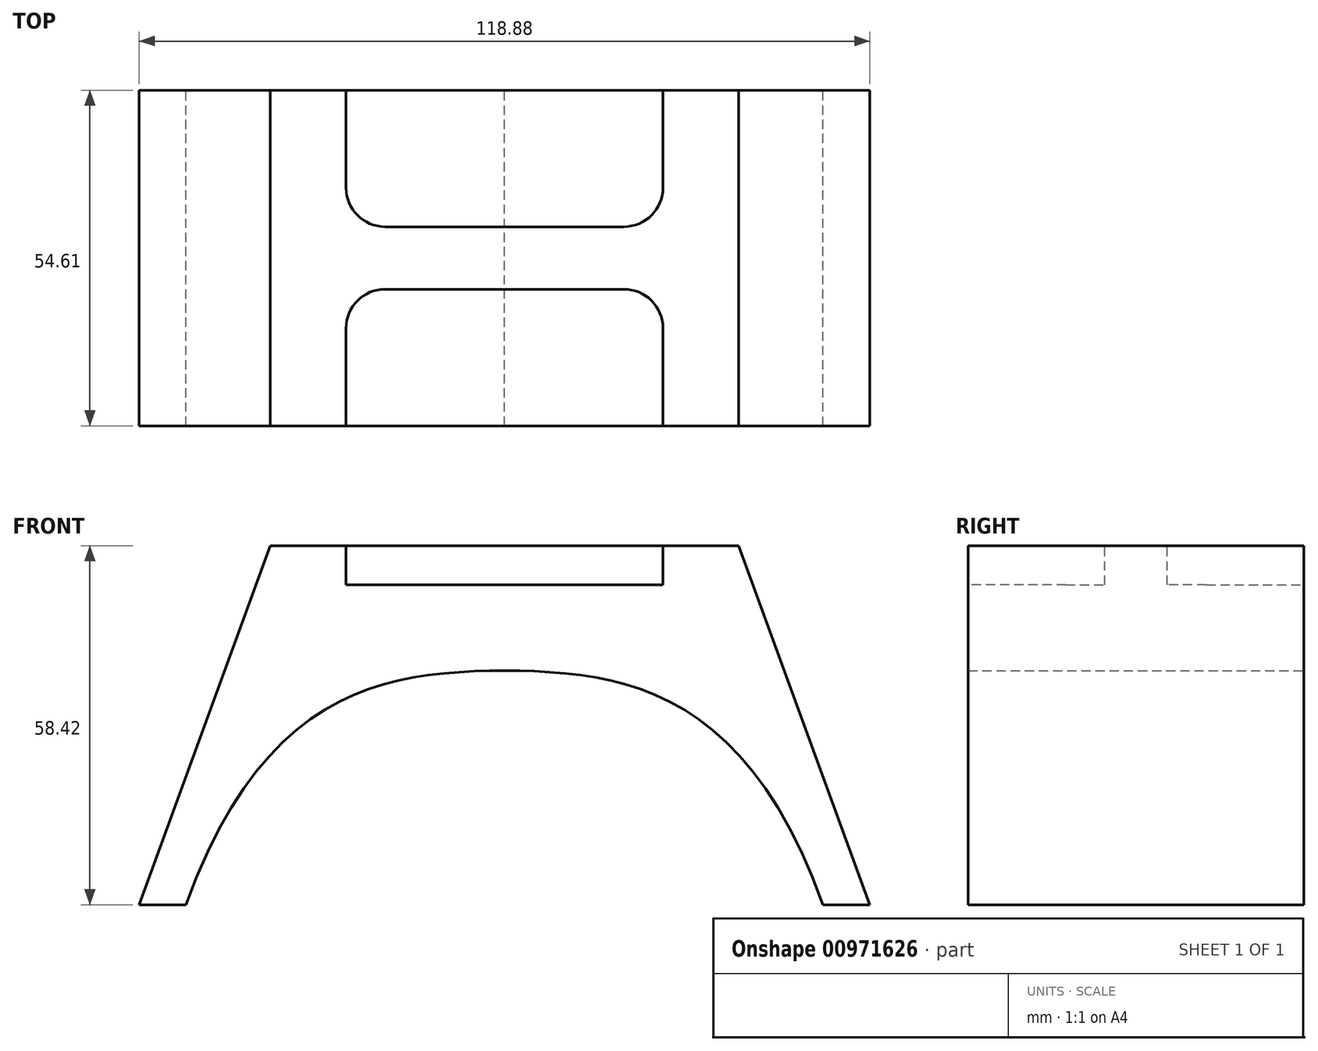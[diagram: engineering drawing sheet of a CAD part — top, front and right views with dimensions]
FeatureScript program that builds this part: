
annotation { "Feature Type Name" : "Feature", "Feature Type Description" : "" }
export const myFeature = defineFeature(function(context is Context, id is Id, definition is map)
    precondition{}
    {
        {
            var Q0;
            Q0=qCreatedBy(makeId("Front.planeOp"),FACE);
            var sketch = newSketch(context, id + "F0", { "sketchPlane" : qUnion([Q0])});
            skLineSegment(sketch, "E0", {"start": v(0, 0) * mm, "end": v(-38.1, 0) * mm});
            skLineSegment(sketch, "E1", {"start": v(-38.1, 0) * mm, "end": v(-59.44, -58.42) * mm});
            skLineSegment(sketch, "E2", {"start": v(-59.44, -58.42) * mm, "end": v(-51.82, -58.42) * mm});
            skLineSegment(sketch, "E3.MirrorCS", {"start": v(0, 0) * mm, "end": v(38.1, 0) * mm});
            skLineSegment(sketch, "E4.MirrorCS", {"start": v(38.1, 0) * mm, "end": v(59.44, -58.42) * mm});
            skLineSegment(sketch, "E5.MirrorCS", {"start": v(59.44, -58.42) * mm, "end": v(51.82, -58.42) * mm});
            skLineSegment(sketch, "E6", {"start": v(0, 0) * mm, "end": v(0, -20.32) * mm, "construction": true});
            skFitSpline(sketch, "E7", {"points": [v(-51.82, -58.42) * mm, v(0, -20.32) * mm], "startDerivative": vector(38.65, 107.28) * mm, "endDerivative": vector(56.07, 0.62) * mm});
            skFitSpline(sketch, "E8.MirrorCS", {"points": [v(51.82, -58.42) * mm, v(0, -20.32) * mm], "startDerivative": vector(-38.65, 107.28) * mm, "endDerivative": vector(-56.07, 0.62) * mm});
            skSolve(sketch);
        }
        {
            var Q0;
            Q0=makeQuery(id+"F0.imprint","IMPRINT",FACE,{"disambiguationData":[TD([[makeQuery(id+"F0.imprint","IMPRINT",EDGE,{"derivedFrom":sQuery(id+"F0.wireOp",EDGE,"E0")}),1.0]])]});
            extrude(context, id + "F1", {"entities" : qUnion([Q0]), "depth" : 54.6 * mm, "offsetDistance" : 25.4 * mm});
        }
        {
            var Q0;
            Q0=makeQuery(id+"F1.opExtrude","SWEPT_FACE",FACE,{"disambiguationData":[OSD([sQuery(id+"F0.wireOp",EDGE,"E0"),sQuery(id+"F0.wireOp",EDGE,"E3.MirrorCS")])]});
            var sketch = newSketch(context, id + "F2", { "sketchPlane" : qUnion([Q0])});
            skLineSegment(sketch, "E9.bottom", {"start": v(19.43, -22.22) * mm, "end": v(-19.43, -22.23) * mm});
            skLineSegment(sketch, "E9.top", {"start": v(25.78, 22.23) * mm, "end": v(-25.78, 22.22) * mm});
            skLineSegment(sketch, "E9.left", {"start": v(25.78, -15.87) * mm, "end": v(25.78, 22.23) * mm});
            skLineSegment(sketch, "E9.right", {"start": v(-25.78, -15.88) * mm, "end": v(-25.78, 22.22) * mm});
            skPoint(sketch, "E9.middle", {"position": v(0, 0) * mm});
            skLineSegment(sketch, "E10.bottom", {"start": v(19.43, -32.39) * mm, "end": v(-19.43, -32.39) * mm});
            skLineSegment(sketch, "E10.top", {"start": v(25.78, -76.84) * mm, "end": v(-25.78, -76.84) * mm});
            skLineSegment(sketch, "E10.left", {"start": v(25.78, -38.74) * mm, "end": v(25.78, -76.84) * mm});
            skLineSegment(sketch, "E10.right", {"start": v(-25.78, -38.74) * mm, "end": v(-25.78, -76.84) * mm});
            skPoint(sketch, "E10.middle", {"position": v(0, -54.61) * mm});
            skPoint(sketch, "E11.visualSharp", {"position": v(-25.78, -22.23) * mm});
            skArc(sketch, "E11.filletArc", {"start": v(-25.78, -15.88) * mm, "mid": v(-23.92, -20.37) * mm, "end": v(-19.43, -22.23) * mm});
            skPoint(sketch, "E12.visualSharp", {"position": v(25.78, -22.22) * mm});
            skArc(sketch, "E12.filletArc", {"start": v(19.43, -22.22) * mm, "mid": v(23.92, -20.37) * mm, "end": v(25.78, -15.87) * mm});
            skPoint(sketch, "E13.visualSharp", {"position": v(25.78, -32.39) * mm});
            skArc(sketch, "E13.filletArc", {"start": v(25.78, -38.74) * mm, "mid": v(23.92, -34.24) * mm, "end": v(19.43, -32.39) * mm});
            skPoint(sketch, "E14.visualSharp", {"position": v(-25.78, -32.39) * mm});
            skArc(sketch, "E14.filletArc", {"start": v(-19.43, -32.39) * mm, "mid": v(-23.92, -34.24) * mm, "end": v(-25.78, -38.74) * mm});
            skSolve(sketch);
        }
        {
            var Q0;
            Q0=makeQuery(id+"F2.imprint","IMPRINT",FACE,{"disambiguationData":[TD([[makeQuery(id+"F2.imprint","IMPRINT",EDGE,{"derivedFrom":sQuery(id+"F2.wireOp",EDGE,"E9.bottom")}),-1.0]])]});
            var Q1;
            Q1=makeQuery(id+"F2.imprint","IMPRINT",FACE,{"disambiguationData":[TD([[makeQuery(id+"F2.imprint","IMPRINT",EDGE,{"derivedFrom":sQuery(id+"F2.wireOp",EDGE,"E10.bottom")}),1.0]])]});
            extrude(context, id + "F3", {"entities" : qUnion([Q0, Q1]), "operationType" : NewBodyOperationType.REMOVE, "oppositeDirection" : true, "depth" : 6.35 * mm, "offsetDistance" : 25.4 * mm});
        }
    });
